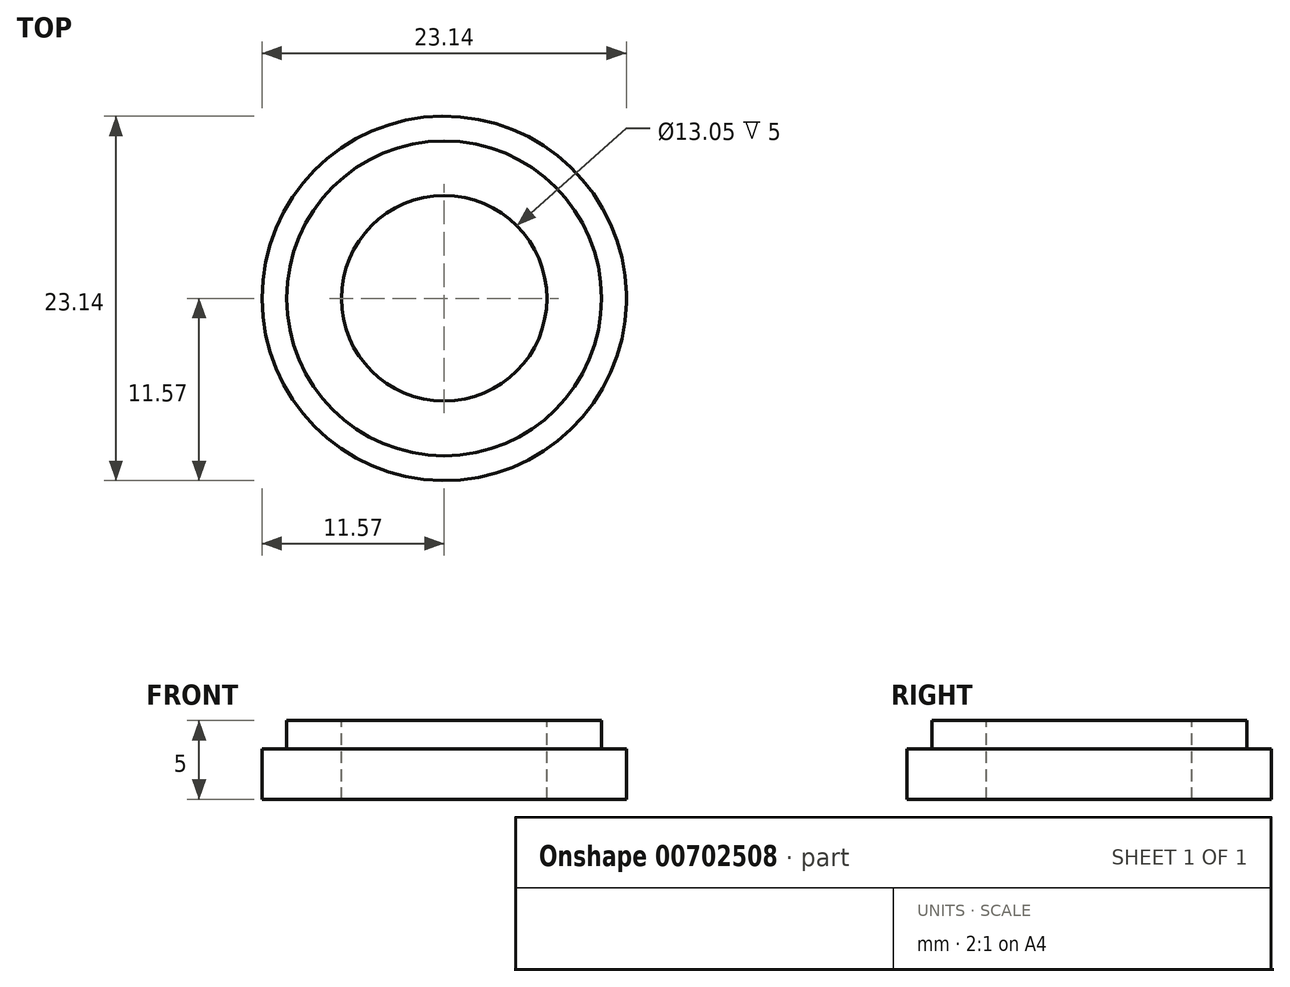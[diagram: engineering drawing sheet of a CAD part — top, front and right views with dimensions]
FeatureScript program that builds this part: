
annotation { "Feature Type Name" : "Feature", "Feature Type Description" : "" }
export const myFeature = defineFeature(function(context is Context, id is Id, definition is map)
    precondition{}
    {
        {
            var Q0;
            Q0=qCreatedBy(makeId("Top.planeOp"),FACE);
            var sketch = newSketch(context, id + "F0", { "sketchPlane" : qUnion([Q0])});
            skCircle(sketch, "E0", {"center": v(0, 0) * mm, "radius": 10 * mm});
            skSolve(sketch);
        }
        {
            var Q0;
            Q0 = qSketchRegion(id + "F0", true);
            extrude(context, id + "F1", {"entities" : qUnion([Q0]), "depth" : 5 * mm, "offsetDistance" : 25 * mm});
        }
        {
            var Q0;
            Q0=makeQuery(id+"F1.opExtrude","CAP_FACE",FACE,{"disambiguationData":[OSD([sQuery(id+"F0.wireOp",EDGE,"E0")])],"isStart":false});
            var sketch = newSketch(context, id + "F2", { "sketchPlane" : qUnion([Q0])});
            skCircle(sketch, "E1", {"center": v(0, 0) * mm, "radius": 6.53 * mm});
            skSolve(sketch);
        }
        {
            var Q0;
            Q0 = qSketchRegion(id + "F2", true);
            extrude(context, id + "F3", {"entities" : qUnion([Q0]), "operationType" : NewBodyOperationType.REMOVE, "oppositeDirection" : true, "depth" : 25 * mm, "offsetDistance" : 25 * mm});
        }
        {
            var Q0;
            Q0=qCreatedBy(makeId("Top.planeOp"),FACE);
            var sketch = newSketch(context, id + "F4", { "sketchPlane" : qUnion([Q0])});
            skLineSegment(sketch, "E2.bottom", {"start": v(8.42, 0.27) * mm, "end": v(11.57, 0.27) * mm});
            skLineSegment(sketch, "E2.top", {"start": v(8.42, -0.27) * mm, "end": v(11.57, -0.27) * mm});
            skLineSegment(sketch, "E2.left", {"start": v(8.42, 0.27) * mm, "end": v(8.42, -0.27) * mm});
            skLineSegment(sketch, "E2.right", {"start": v(11.57, 0.27) * mm, "end": v(11.57, -0.27) * mm});
            skPoint(sketch, "E2.middle", {"position": v(10, 0) * mm});
            skSolve(sketch);
        }
        {
            var Q0;
            Q0 = qSketchRegion(id + "F4", true);
            extrude(context, id + "F5", {"entities" : qUnion([Q0]), "operationType" : NewBodyOperationType.ADD, "depth" : 3.2 * mm, "offsetDistance" : 25 * mm});
        }
        {
            var Q0;
            Q0=makeQuery(id+"F5.opExtrude","SWEPT_FACE",FACE,{"disambiguationData":[OSD([sQuery(id+"F4.wireOp",EDGE,"E2.top")])]});
            var Q1;
            Q1=sQuery(id+"F0.wireOp",EDGE,"E0");
            revolve(context, id + "F6", {"operationType" : NewBodyOperationType.ADD, "surfaceOperationType" : NewSurfaceOperationType.NEW, "entities" : qUnion([Q0]), "axis" : qUnion([Q1]), "revolveType" : RevolveType.FULL});
        }
    });
